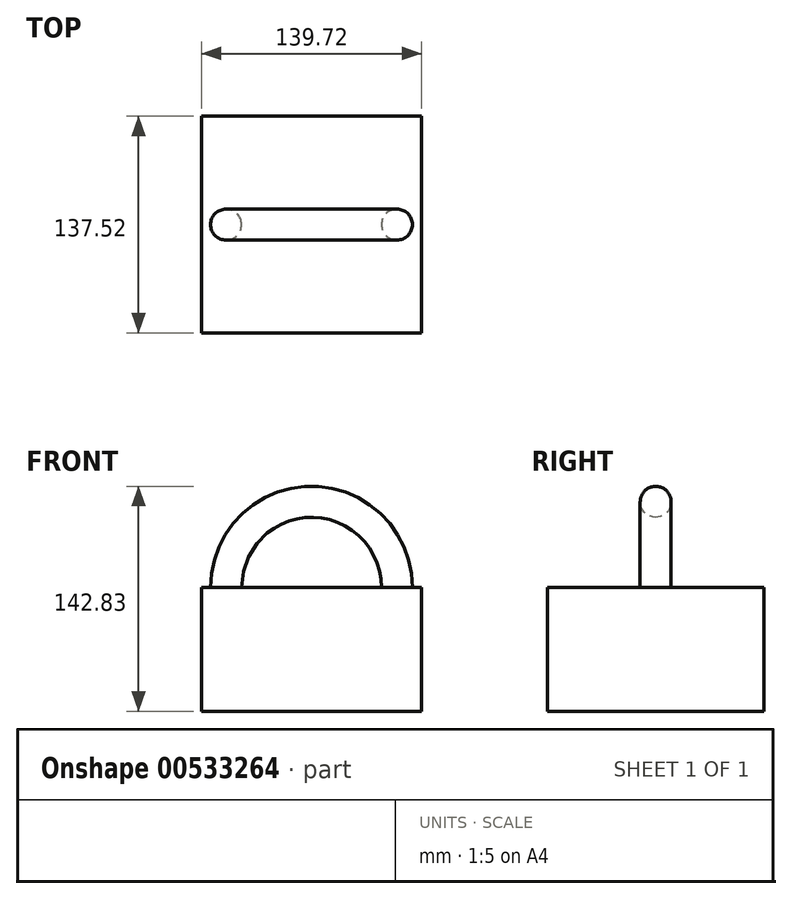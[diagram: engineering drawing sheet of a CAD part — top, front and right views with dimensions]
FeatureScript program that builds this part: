
annotation { "Feature Type Name" : "Feature", "Feature Type Description" : "" }
export const myFeature = defineFeature(function(context is Context, id is Id, definition is map)
    precondition{}
    {
        {
            var Q0;
            Q0=qCreatedBy(makeId("Top.planeOp"),FACE);
            var sketch = newSketch(context, id + "F0", { "sketchPlane" : qUnion([Q0])});
            skLineSegment(sketch, "E0.bottom", {"start": v(69.86, -68.76) * mm, "end": v(-69.86, -68.76) * mm});
            skLineSegment(sketch, "E0.top", {"start": v(69.86, 68.76) * mm, "end": v(-69.86, 68.76) * mm});
            skLineSegment(sketch, "E0.left", {"start": v(69.86, -68.76) * mm, "end": v(69.86, 68.76) * mm});
            skLineSegment(sketch, "E0.right", {"start": v(-69.86, -68.76) * mm, "end": v(-69.86, 68.76) * mm});
            skPoint(sketch, "E0.middle", {"position": v(0, 0) * mm});
            skLineSegment(sketch, "E1", {"start": v(0, 68.76) * mm, "end": v(0, -68.76) * mm});
            skSolve(sketch);
        }
        {
            var Q0;
            Q0=qCreatedBy(makeId("Top.planeOp"),FACE);
            var sketch = newSketch(context, id + "F1", { "sketchPlane" : qUnion([Q0])});
            skCircle(sketch, "E2", {"center": v(54.26, 0) * mm, "radius": 9.82 * mm});
            skSolve(sketch);
        }
        {
            var Q0;
            {var subQ0=sQuery(id+"F0.wireOp",EDGE,"E0.right");Q0=makeQuery(id+"F0.imprint","IMPRINT",FACE,{"disambiguationData":[TD([[makeQuery(id+"F0.imprint","IMPRINT",EDGE,{"derivedFrom":subQ0}),-1.0]])]});}
            var Q1;
            {var subQ0=sQuery(id+"F0.wireOp",EDGE,"E0.left");Q1=makeQuery(id+"F0.imprint","IMPRINT",FACE,{"disambiguationData":[TD([[makeQuery(id+"F0.imprint","IMPRINT",EDGE,{"derivedFrom":subQ0}),1.0]])]});}
            extrude(context, id + "F2", {"entities" : qUnion([Q0, Q1]), "oppositeDirection" : true, "depth" : 78.74 * mm, "offsetDistance" : 25.4 * mm});
        }
        {
            var Q0;
            Q0=makeQuery(id+"F1.imprint","IMPRINT",FACE,{"disambiguationData":[TD([[makeQuery(id+"F1.imprint","IMPRINT",EDGE,{"derivedFrom":sQuery(id+"F1.wireOp",EDGE,"E2")}),1.0]])]});
            var Q1;
            Q1=sQuery(id+"F0.wireOp",EDGE,"E1");
            revolve(context, id + "F3", {"operationType" : NewBodyOperationType.ADD, "entities" : qUnion([Q0]), "axis" : qUnion([Q1]), "revolveType" : RevolveType.FULL});
        }
    });
